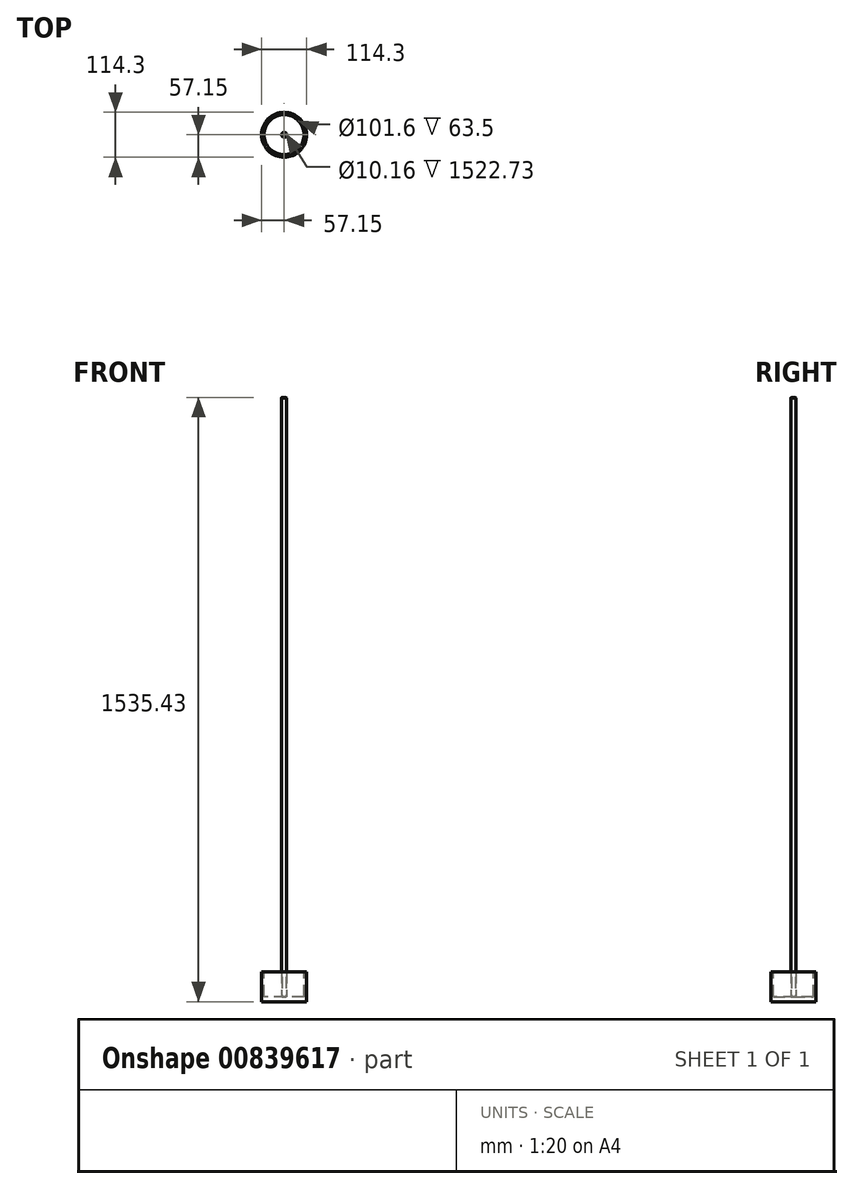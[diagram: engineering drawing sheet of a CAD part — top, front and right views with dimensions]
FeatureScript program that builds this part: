
annotation { "Feature Type Name" : "Feature", "Feature Type Description" : "" }
export const myFeature = defineFeature(function(context is Context, id is Id, definition is map)
    precondition{}
    {
        {
            var Q0;
            Q0=qCreatedBy(makeId("Top.planeOp"),FACE);
            var sketch = newSketch(context, id + "F0", { "sketchPlane" : qUnion([Q0])});
            skCircle(sketch, "E0", {"center": v(0, 0) * mm, "radius": 57.15 * mm});
            skSolve(sketch);
        }
        {
            var Q0;
            Q0 = qSketchRegion(id + "F0", true);
            extrude(context, id + "F1", {"entities" : qUnion([Q0]), "depth" : 76.2 * mm, "offsetDistance" : 25.4 * mm});
        }
        {
            var Q0;
            Q0=makeQuery(id+"F1.opExtrude","CAP_FACE",FACE,{"disambiguationData":[OSD([sQuery(id+"F0.wireOp",EDGE,"E0")])],"isStart":false});
            var sketch = newSketch(context, id + "F2", { "sketchPlane" : qUnion([Q0])});
            skCircle(sketch, "E1", {"center": v(0, 0) * mm, "radius": 50.8 * mm});
            skSolve(sketch);
        }
        {
            var Q0;
            Q0 = qSketchRegion(id + "F2", true);
            extrude(context, id + "F3", {"entities" : qUnion([Q0]), "operationType" : NewBodyOperationType.REMOVE, "oppositeDirection" : true, "depth" : 63.5 * mm, "offsetDistance" : 25.4 * mm});
        }
        {
            var Q0;
            Q0=makeQuery(id+"F3.boolean.opBoolean","COPY",FACE,{"derivedFrom":makeQuery(id+"F3.opExtrude","CAP_FACE",FACE,{"disambiguationData":[OSD([sQuery(id+"F2.wireOp",EDGE,"E1")])],"isStart":false})});
            var sketch = newSketch(context, id + "F4", { "sketchPlane" : qUnion([Q0])});
            skCircle(sketch, "E2", {"center": v(0, 0) * mm, "radius": 6.35 * mm});
            skCircle(sketch, "E3", {"center": v(0, 0) * mm, "radius": 5.08 * mm});
            skSolve(sketch);
        }
        {
            var Q0;
            Q0 = qSketchRegion(id + "F4", true);
            extrude(context, id + "F5", {"entities" : qUnion([Q0]), "operationType" : NewBodyOperationType.ADD, "depth" : 1524 * mm, "offsetDistance" : 25.4 * mm});
        }
        {
            var Q0;
            Q0=makeQuery(id+"F5.opExtrude","CAP_EDGE",EDGE,{"disambiguationData":[OSD([sQuery(id+"F4.wireOp",EDGE,"E2")])],"isStart":false});
            chamfer(context, id + "F6", {"entities" : qUnion([Q0]), "width" : 2.54 * mm, "tangentPropagation" : true});
        }
    });
